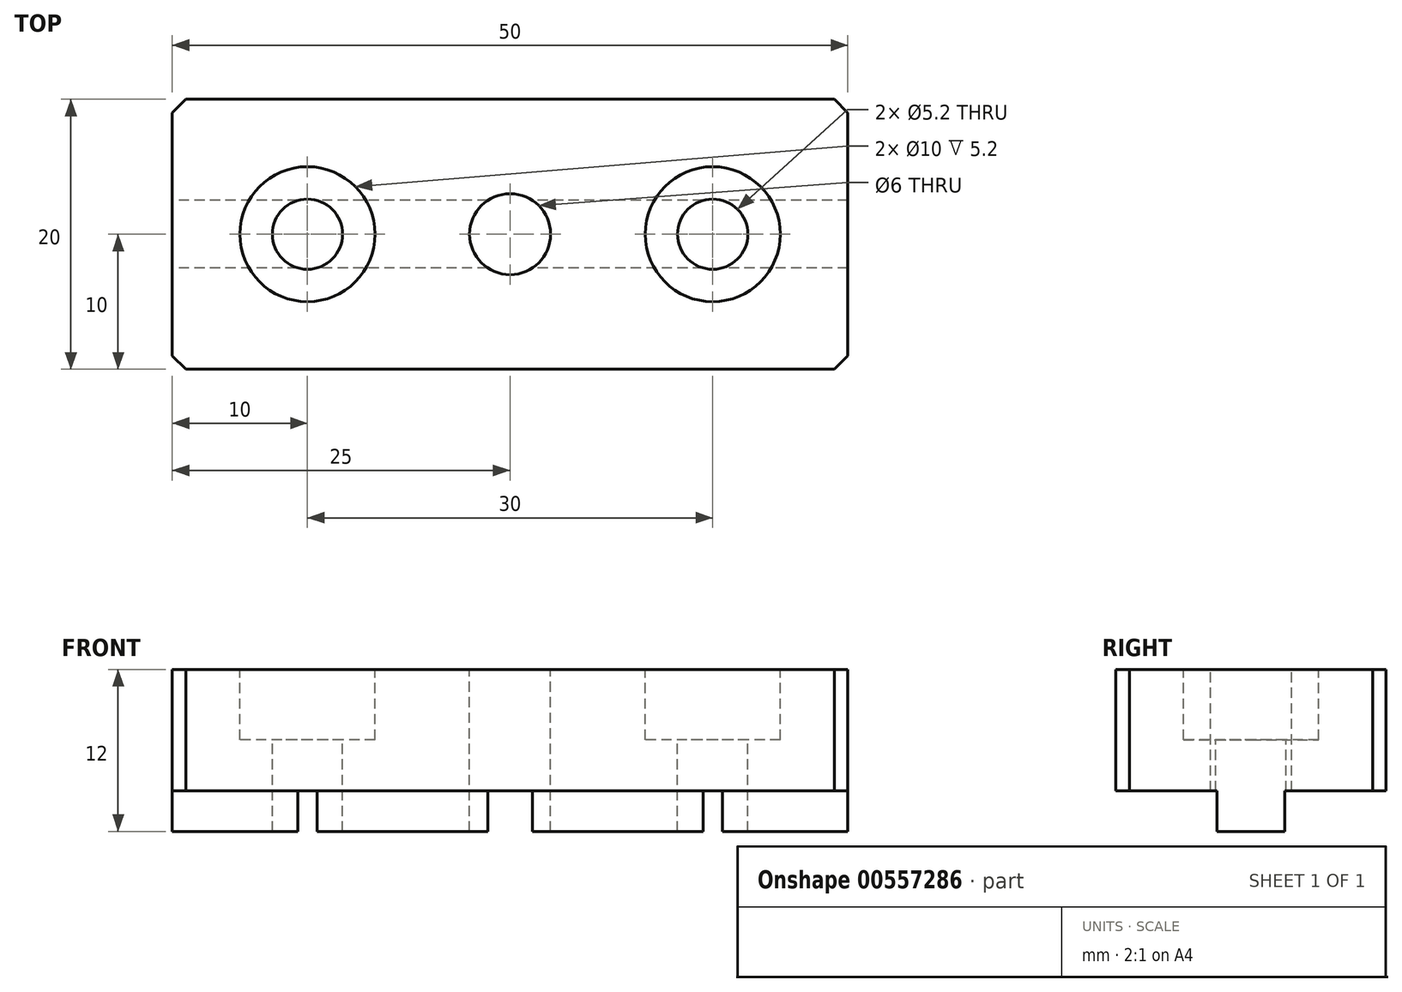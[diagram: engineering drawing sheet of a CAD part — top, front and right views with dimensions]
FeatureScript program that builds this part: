
annotation { "Feature Type Name" : "Feature", "Feature Type Description" : "" }
export const myFeature = defineFeature(function(context is Context, id is Id, definition is map)
    precondition{}
    {
        {
            var Q0;
            Q0=qCreatedBy(makeId("Right.planeOp"),FACE);
            var sketch = newSketch(context, id + "F0", { "sketchPlane" : qUnion([Q0])});
            skLineSegment(sketch, "E0.bottom", {"start": v(-10, 4.5) * mm, "end": v(10, 4.5) * mm});
            skLineSegment(sketch, "E0.top", {"start": v(-10, -4.5) * mm, "end": v(-2.5, -4.5) * mm});
            skLineSegment(sketch, "E0.left", {"start": v(-10, 4.5) * mm, "end": v(-10, -4.5) * mm});
            skLineSegment(sketch, "E0.right", {"start": v(10, 4.5) * mm, "end": v(10, -4.5) * mm});
            skPoint(sketch, "E0.middle", {"position": v(0, 0) * mm});
            skLineSegment(sketch, "E1", {"start": v(-2.5, -4.5) * mm, "end": v(-2.5, -7.5) * mm});
            skLineSegment(sketch, "E2", {"start": v(-2.5, -7.5) * mm, "end": v(2.5, -7.5) * mm});
            skLineSegment(sketch, "E3", {"start": v(2.5, -7.5) * mm, "end": v(2.5, -4.5) * mm});
            skLineSegment(sketch, "E4.trimOffspring", {"start": v(2.5, -4.5) * mm, "end": v(10, -4.5) * mm});
            skSolve(sketch);
        }
        {
            var Q0;
            Q0=makeQuery(id+"F0.imprint","IMPRINT",FACE,{"disambiguationData":[TD([[makeQuery(id+"F0.imprint","IMPRINT",EDGE,{"derivedFrom":sQuery(id+"F0.wireOp",EDGE,"E0.bottom")}),-1.0]])]});
            extrude(context, id + "F1", {"entities" : qUnion([Q0]), "endBound" : BoundingType.SYMMETRIC, "depth" : 50 * mm, "offsetDistance" : 25 * mm});
        }
        {
            var Q0;
            Q0=makeQuery(id+"F1.opExtrude","SWEPT_FACE",FACE,{"disambiguationData":[OSD([sQuery(id+"F0.wireOp",EDGE,"E0.bottom")])]});
            var sketch = newSketch(context, id + "F2", { "sketchPlane" : qUnion([Q0])});
            skPoint(sketch, "E5", {"position": v(0, 0) * mm});
            skPoint(sketch, "E6", {"position": v(-15, 0) * mm});
            skPoint(sketch, "E7", {"position": v(15, 0) * mm});
            skSolve(sketch);
        }
        {
            var Q0;
            Q0=sQuery(id+"F2.wireOp",VERTEX,"E6");
            var Q1;
            Q1=sQuery(id+"F2.wireOp",VERTEX,"E7");
            var Q2;
            Q2=makeQuery(id+"F1.opExtrude","SWEPT_BODY",BODY,{"disambiguationData":[OSD([sQuery(id+"F0.wireOp",EDGE,"E0.bottom"),sQuery(id+"F0.wireOp",EDGE,"E0.top"),sQuery(id+"F0.wireOp",EDGE,"E0.left"),sQuery(id+"F0.wireOp",EDGE,"E0.right"),sQuery(id+"F0.wireOp",EDGE,"E1"),sQuery(id+"F0.wireOp",EDGE,"E2"),sQuery(id+"F0.wireOp",EDGE,"E3"),sQuery(id+"F0.wireOp",EDGE,"E4.trimOffspring")])]});
            hole(context, id + "F3", {"style" : HoleStyle.C_BORE, "endStyle" : HoleEndStyle.THROUGH, "holeDiameter" : 5.2 * mm, "cBoreDiameter" : 10 * mm, "cBoreDepth" : 5.2 * mm, "isTappedThrough" : true, "tappedDepth" : 12 * mm, "tapClearance" : 3, "startFromSketch" : true, "locations" : qUnion([Q0, Q1]), "scope" : qUnion([Q2])});
        }
        {
            var Q0;
            Q0=sQuery(id+"F2.wireOp",VERTEX,"E5");
            var Q1;
            Q1=makeQuery(id+"F1.opExtrude","SWEPT_BODY",BODY,{"disambiguationData":[OSD([sQuery(id+"F0.wireOp",EDGE,"E0.bottom"),sQuery(id+"F0.wireOp",EDGE,"E0.top"),sQuery(id+"F0.wireOp",EDGE,"E0.left"),sQuery(id+"F0.wireOp",EDGE,"E0.right"),sQuery(id+"F0.wireOp",EDGE,"E1"),sQuery(id+"F0.wireOp",EDGE,"E2"),sQuery(id+"F0.wireOp",EDGE,"E3"),sQuery(id+"F0.wireOp",EDGE,"E4.trimOffspring")])]});
            hole(context, id + "F4", {"style" : HoleStyle.SIMPLE, "endStyle" : HoleEndStyle.THROUGH, "holeDiameter" : 6 * mm, "isTappedThrough" : true, "tappedDepth" : 12 * mm, "tapClearance" : 3, "startFromSketch" : true, "locations" : qUnion([Q0]), "scope" : qUnion([Q1])});
        }
        {
            var Q0;
            Q0=makeQuery(id+"F1.opExtrude","CAP_EDGE",EDGE,{"disambiguationData":[OSD([sQuery(id+"F0.wireOp",EDGE,"E0.left")])],"isStart":false});
            var Q1;
            Q1=makeQuery(id+"F1.opExtrude","CAP_EDGE",EDGE,{"disambiguationData":[OSD([sQuery(id+"F0.wireOp",EDGE,"E0.right")])],"isStart":false});
            var Q2;
            Q2=makeQuery(id+"F1.opExtrude","CAP_EDGE",EDGE,{"disambiguationData":[OSD([sQuery(id+"F0.wireOp",EDGE,"E0.left")])],"isStart":true});
            var Q3;
            Q3=makeQuery(id+"F1.opExtrude","CAP_EDGE",EDGE,{"disambiguationData":[OSD([sQuery(id+"F0.wireOp",EDGE,"E0.right")])],"isStart":true});
            chamfer(context, id + "F5", {"entities" : qUnion([Q0, Q1, Q2, Q3]), "width" : 1 * mm, "tangentPropagation" : true});
        }
    });
